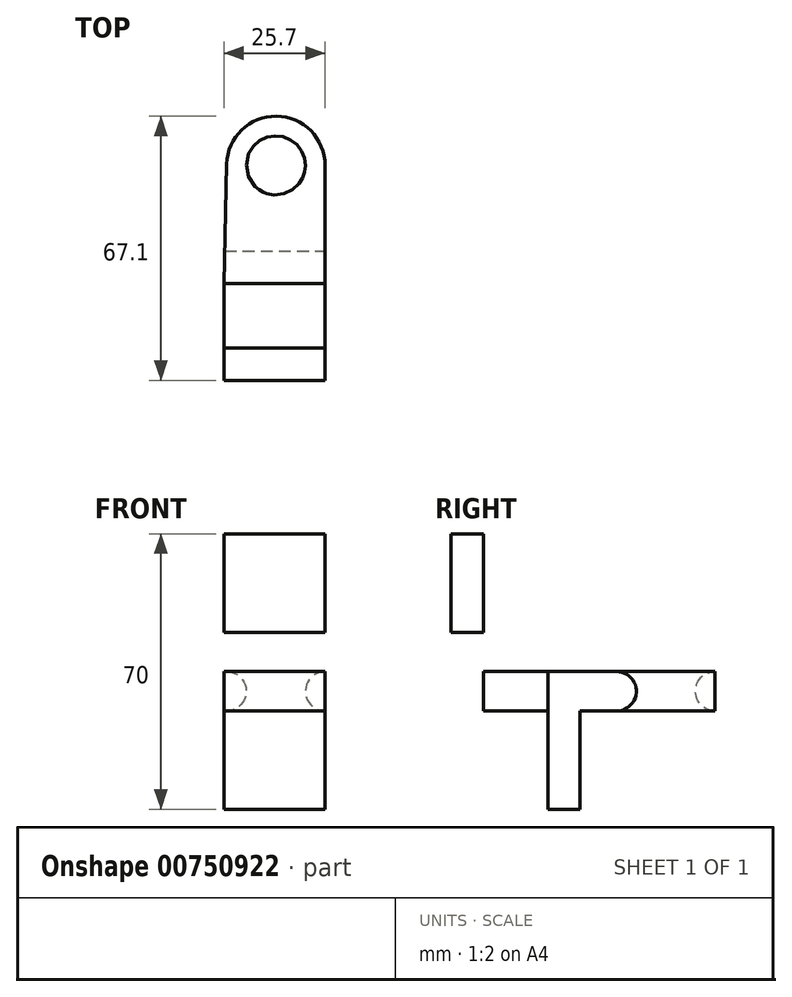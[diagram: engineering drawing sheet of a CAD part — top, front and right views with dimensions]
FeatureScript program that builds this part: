
annotation { "Feature Type Name" : "Feature", "Feature Type Description" : "" }
export const myFeature = defineFeature(function(context is Context, id is Id, definition is map)
    precondition{}
    {
        {
            var Q0;
            Q0=qCreatedBy(makeId("Top.planeOp"),FACE);
            var sketch = newSketch(context, id + "F0", { "sketchPlane" : qUnion([Q0])});
            skCircle(sketch, "E0", {"center": v(0, 0) * mm, "radius": 7.5 * mm});
            skArc(sketch, "E1", {"start": v(12.5, 0) * mm, "mid": v(0.15, 12.5) * mm, "end": v(-12.5, 0.3) * mm});
            skLineSegment(sketch, "E2", {"start": v(-12.5, 0.3) * mm, "end": v(-13.2, -30) * mm});
            skLineSegment(sketch, "E3", {"start": v(12.5, 0) * mm, "end": v(12.5, -30) * mm});
            skLineSegment(sketch, "E4", {"start": v(12.5, -30) * mm, "end": v(-13.2, -30) * mm});
            skSolve(sketch);
        }
        {
            var Q0;
            Q0 = qSketchRegion(id + "F0", true);
            extrude(context, id + "F1", {"entities" : qUnion([Q0]), "depth" : 10 * mm, "offsetDistance" : 25 * mm});
        }
        {
            var Q0;
            Q0=makeQuery(id+"F1.opExtrude","CAP_EDGE",EDGE,{"disambiguationData":[OSD([sQuery(id+"F0.wireOp",EDGE,"E0")])],"isStart":false});
            var Q1;
            Q1=makeQuery(id+"F1.opExtrude","CAP_EDGE",EDGE,{"disambiguationData":[OSD([sQuery(id+"F0.wireOp",EDGE,"E0")])],"isStart":true});
            fillet(context, id + "F2", {"entities" : qUnion([Q0, Q1]), "radius" : 5 * mm, "tangentPropagation" : true, "allowEdgeOverflow" : false});
        }
        {
            var Q0;
            Q0=makeQuery(id+"F1.opExtrude","CAP_FACE",FACE,{"disambiguationData":[OSD([sQuery(id+"F0.wireOp",EDGE,"E0"),sQuery(id+"F0.wireOp",EDGE,"E1"),sQuery(id+"F0.wireOp",EDGE,"E2"),sQuery(id+"F0.wireOp",EDGE,"E3"),sQuery(id+"F0.wireOp",EDGE,"E4")])],"isStart":true});
            var sketch = newSketch(context, id + "F3", { "sketchPlane" : qUnion([Q0])});
            skLineSegment(sketch, "E5.bottom", {"start": v(-13.2, 30) * mm, "end": v(12.5, 30) * mm});
            skLineSegment(sketch, "E5.top", {"start": v(-13.2, 21.8) * mm, "end": v(12.5, 21.8) * mm});
            skLineSegment(sketch, "E5.left", {"start": v(-13.2, 30) * mm, "end": v(-13.2, 21.8) * mm});
            skLineSegment(sketch, "E5.right", {"start": v(12.5, 30) * mm, "end": v(12.5, 21.8) * mm});
            skLineSegment(sketch, "E6.top", {"start": v(-13.2, 38.2) * mm, "end": v(12.5, 38.2) * mm});
            skLineSegment(sketch, "E6.left", {"start": v(-13.2, 30) * mm, "end": v(-13.2, 38.2) * mm});
            skLineSegment(sketch, "E6.right", {"start": v(12.5, 30) * mm, "end": v(12.5, 38.2) * mm});
            skLineSegment(sketch, "E7.top", {"start": v(-13.2, 46.4) * mm, "end": v(12.5, 46.4) * mm});
            skLineSegment(sketch, "E7.left", {"start": v(-13.2, 38.2) * mm, "end": v(-13.2, 46.4) * mm});
            skLineSegment(sketch, "E7.right", {"start": v(12.5, 38.2) * mm, "end": v(12.5, 46.4) * mm});
            skSolve(sketch);
        }
        {
            var Q0;
            {var subQ0=sQuery(id+"F3.wireOp",EDGE,"E5.right");Q0=makeQuery(id+"F3.imprint","IMPRINT",FACE,{"disambiguationData":[TD([[makeQuery(id+"F3.imprint","IMPRINT",EDGE,{"derivedFrom":subQ0}),1.0]])]});}
            var Q1;
            Q1=makeQuery(id+"F3.imprint","IMPRINT",FACE,{"disambiguationData":[TD([[makeQuery(id+"F3.imprint","IMPRINT",EDGE,{"derivedFrom":sQuery(id+"F3.wireOp",EDGE,"E6.top")}),1.0]])]});
            extrude(context, id + "F4", {"entities" : qUnion([Q0, Q1]), "operationType" : NewBodyOperationType.ADD, "depth" : 25 * mm, "offsetDistance" : 25 * mm});
        }
        {
            var Q0;
            Q0=makeQuery(id+"F3.imprint","IMPRINT",FACE,{"disambiguationData":[TD([[makeQuery(id+"F3.imprint","IMPRINT",EDGE,{"derivedFrom":sQuery(id+"F3.wireOp",EDGE,"E5.bottom")}),-1.0]])]});
            var Q1;
            Q1=makeQuery(id+"F3.imprint","IMPRINT",FACE,{"disambiguationData":[TD([[makeQuery(id+"F3.imprint","IMPRINT",EDGE,{"derivedFrom":sQuery(id+"F3.wireOp",EDGE,"E6.top")}),1.0]])]});
            var Q2;
            Q2=makeQuery(id+"F1.opExtrude","CAP_FACE",FACE,{"disambiguationData":[OSD([sQuery(id+"F0.wireOp",EDGE,"E0"),sQuery(id+"F0.wireOp",EDGE,"E1"),sQuery(id+"F0.wireOp",EDGE,"E2"),sQuery(id+"F0.wireOp",EDGE,"E3"),sQuery(id+"F0.wireOp",EDGE,"E4")])],"isStart":false});
            extrude(context, id + "F5", {"entities" : qUnion([Q0, Q1]), "endBound" : BoundingType.UP_TO_SURFACE, "oppositeDirection" : true, "depth" : 25 * mm, "endBoundEntityFace" : qUnion([Q2]), "offsetDistance" : 25 * mm});
        }
        {
            var Q0;
            Q0=makeQuery(id+"F4.opExtrude","SWEPT_BODY",BODY,{"disambiguationData":[OSD([sQuery(id+"F3.wireOp",EDGE,"E6.top"),sQuery(id+"F3.wireOp",EDGE,"E7.top"),sQuery(id+"F3.wireOp",EDGE,"E7.left"),sQuery(id+"F3.wireOp",EDGE,"E7.right")])]});
            var Q1;
            Q1=makeQuery(id+"F5.opExtrude","CAP_EDGE",EDGE,{"disambiguationData":[OSD([sQuery(id+"F3.wireOp",EDGE,"E7.top")])],"isStart":false});
            transform(context, id + "F6", {"entities" : qUnion([Q0]), "transformType" : TransformType.ROTATION, "transformAxis" : qUnion([Q1]), "angle" : 180 * degree, "makeCopy" : false});
        }
    });
